# Revit family: PDU metered 1U
name_source: partatom
category: Installations électriques
units: mm (PartAtom-declared; Revit-internal decimal feet)

## family parameters
Basée sur le plan de construction = Non
Conserver l'orientation des annotations = Non
Cote de connecteur circulaire = Utiliser le diamètre
Couper avec des vides une fois chargée = Non
Numéro OmniClass = 23.80.00.00
Partagée = Non
Point de calcul de pièce = Non
Titre OmniClass = Electric Power and Lighting
Toujours verticalement = Oui
Type d'élément = Normal

## types (2) — shared parameters
Classe d'application = EC002762
Connectable par box internet = Oui
Consommation en veille = 0 mA
Couleur = Noir
Courant d'alimentation = 16-16
Description = PDU metered base 19 inch 1 phase 16A 12 C13 locking outlets IEC-320 C20
Elévation par défaut = 1000 mm  [stored 3.28084 ft]
Fabricant = LEGRAND
Fonction = Unité DE DISTRIBUTION D'ENERGIE
Fréquence d'alimentation = 50-50
IP = IP40
Largeur (mm) = 483 mm
Libellé BIM = Linkeo DATA CENTER BASIC PDU
Lien e-catalogue = https://www.legrand.fr
Longueur = 45 mm
Marquage = Non
Nombre de phases = 1
Nombre de prises C13 = 8
Profondeur (mm) = 115 mm  [stored 0.377297 ft]
Profondeur cuve + capot = 115 mm  [stored 0.377297 ft]
Programmable = Appli Web
RAL = 9017
Sens de montage = Horizontal
Type d'alimentation = C20
Type de tension = AC
zero-valued in all types: Nombre de disjoncteurs, Nombre de prises C19

## per-type parameters (varying)
| type | Base_Node | EAN | Référence Legrand |
| PDU MB 19P 1P 16A 12 C13 | Base_Node_Horizontal : Base HD | 3414972245852 | LG-646100 |
| PDU MN 19P 1P 16A 12 C13 | Base_Node_Horizontal : Node HD | 3414972245913 | LG-646101 |

note: [stored X ft] marks values corroborated as IEEE doubles in the binary element streams (Revit-internal decimal feet)
